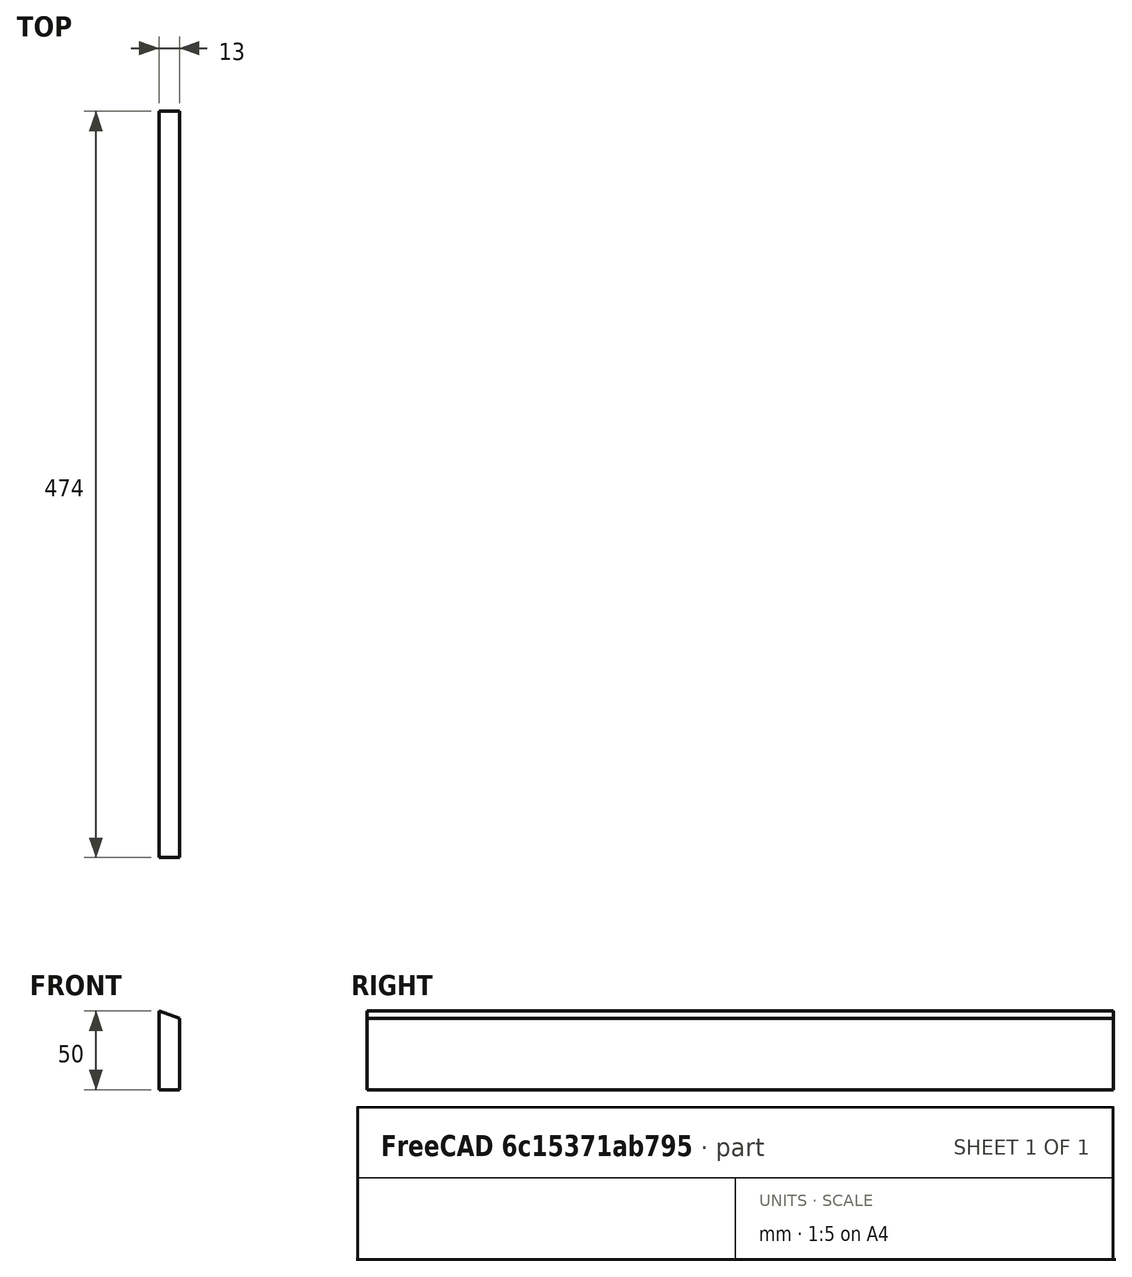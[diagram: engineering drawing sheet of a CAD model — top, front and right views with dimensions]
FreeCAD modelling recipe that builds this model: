
FCSTD DOCUMENT  (FreeCAD 0.19R24276 (Git))
Label: 4000_Body_front_base_YZ
License: All rights reserved
LicenseURL: http://en.wikipedia.org/wiki/All_rights_reserved
objects: Spreadsheet::Sheet×1, Sketcher::SketchObject×1, PartDesign::Pad×1, PartDesign::Body×1
note: 4 computed .brp shape members not serialized (recipe doc carries the construction recipe); baked Part::Feature solids carry a one-line shape summary decoded from their .brp

FEATURE [Spreadsheet::Sheet] Spreadsheet  label="xls"
  cells = B5=BODY FRONT; E5=nominal size; B6=Board Thickness; C6(thickness)=13; D6=xls.thickness; B7=Horizontal Y; C7(width)==+E7 - 2 * C6; D7=xls.width; E7=500; B8=X=; C8(height)=50; D8=xls.height; B9=Angle Y; C9(tilt)=90; D9=xls.tilt
FEATURE [Sketcher::SketchObject] Sketch
  FullyConstrained = false
  MapMode = 5
  Placement = pos=(0,0,0) rot=(1,0,0;1.5708rad)
  Support = -> [XZ_Plane]
  expr: Constraints[5] = <<xls>>.thickness
  expr: Constraints[6] = <<xls>>.tilt
  expr: Constraints[9] = <<xls>>.height
  sketch-geometry (4):
    g0: LineSegment StartX=13 StartY=-1.4345e-12 StartZ=0 EndX=13 EndY=45.2684 EndZ=0
    g1: LineSegment StartX=13 StartY=45.2684 StartZ=0 EndX=8.5603e-12 EndY=50 EndZ=0
    g2: LineSegment StartX=8.5603e-12 StartY=50 StartZ=0 EndX=0 EndY=0 EndZ=0
    g3: LineSegment StartX=0 StartY=0 StartZ=0 EndX=13 EndY=-1.4345e-12 EndZ=0
  constraints (11):
    c: Coincident(g0,g1)
    c: Coincident(g1,g2)
    c: Coincident(g2,g3)
    c: Parallel(g0,g2)
    c: Perpendicular(g0,g3)
    c: Distance(g3) = 13
    c: Angle(g-1,g0) = 1.5708
    c: Coincident(g0,g3)
    c: Coincident(g-1,g2)
    c: DistanceY(g2,g2) = 50
    c: Angle(g1,g0) = 1.91986
FEATURE [PartDesign::Pad] Pad
  AllowMultiFace = false
  Direction = (1,1,1)
  Length = 474
  Length2 = 100
  Placement = pos=(0,0,0) rot=(1,0,0;1.5708rad)
  Profile = -> Sketch
  Reversed = true
  Type = 0
  expr: Length = <<xls>>.width
FEATURE [PartDesign::Body] Body
  Group = -> [Sketch,Pad]
  Origin = -> Origin
  Tip = -> Pad
